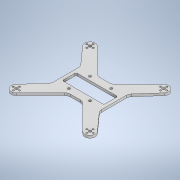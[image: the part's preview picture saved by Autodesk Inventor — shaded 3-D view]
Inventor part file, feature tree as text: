
AUTODESK INVENTOR PART (.ipt)
format: ipt  version: 2021 (Build 250183000, 183)  size: 247,296 bytes
history: native  units: in
note: dims shown in document units (in); Inventor stores cm internally (conversion verified against a paired STEP export)
features: sketch x2, fillet x2, extrude x1
ambient origin geometry x8: Origin, YZ Plane, XZ Plane, XY Plane, X Axis, Y Axis, Z Axis, Center Point
bodies: Body1 (feature_tree)
feature tree (5):
  sketch  "Sketch1"  dims[d0=1.2008in d1=1.2008in d2=0.1378in d3=0.1378in]
  extrude  "Extrusion2"  Depth=0.1378in
  fillet  "Fillet1"  Radius=0.1378in
  fillet  "Fillet2"  Radius=0.1378in
  sketch  "Sketch2"  dims[d4=0.1378in d5=0.1378in d6=1.6535in d7=0.1969in d8=0.1969in d9=0.1969in d10=0.1969in d11=1.7717in d14=2.3622in d15=0.7874in d16=0.1969in d17=0.1969in d20=2.9528in d21=2.9528in d22=2.9528in d23=2.5591in d24=2.5591in d25=2.5591in d26=2.5591in d27=2.9528in d28=0.5906in d29=0.5906in d31=0.5906in d32=0.5906in d33=2.7165in d34=1.6535in d35=1.2008in d36=1.2008in d37=0.1378in d38=0.1378in d39=0.1378in d40=0.1378in d41=0.3543in d42=0.3543in d43=0.3543in d44=0.3543in d45=0.0984in d46=0.0984in d47=0.0984in d48=0.0984in d49=0.0984in d50=0.0984in d51=0.0984in d52=0.0984in d53=0.0984in d54=0.0984in d55=0.0984in d56=0.0984in d57=0.0984in d58=0.0984in d59=0.0984in d60=0.0984in d61=0.1575in d62=0.1575in d63=0.1575in d64=0.1575in d65=0.1378in d66=0.0in d67=0.315in d68=0.0787in]
